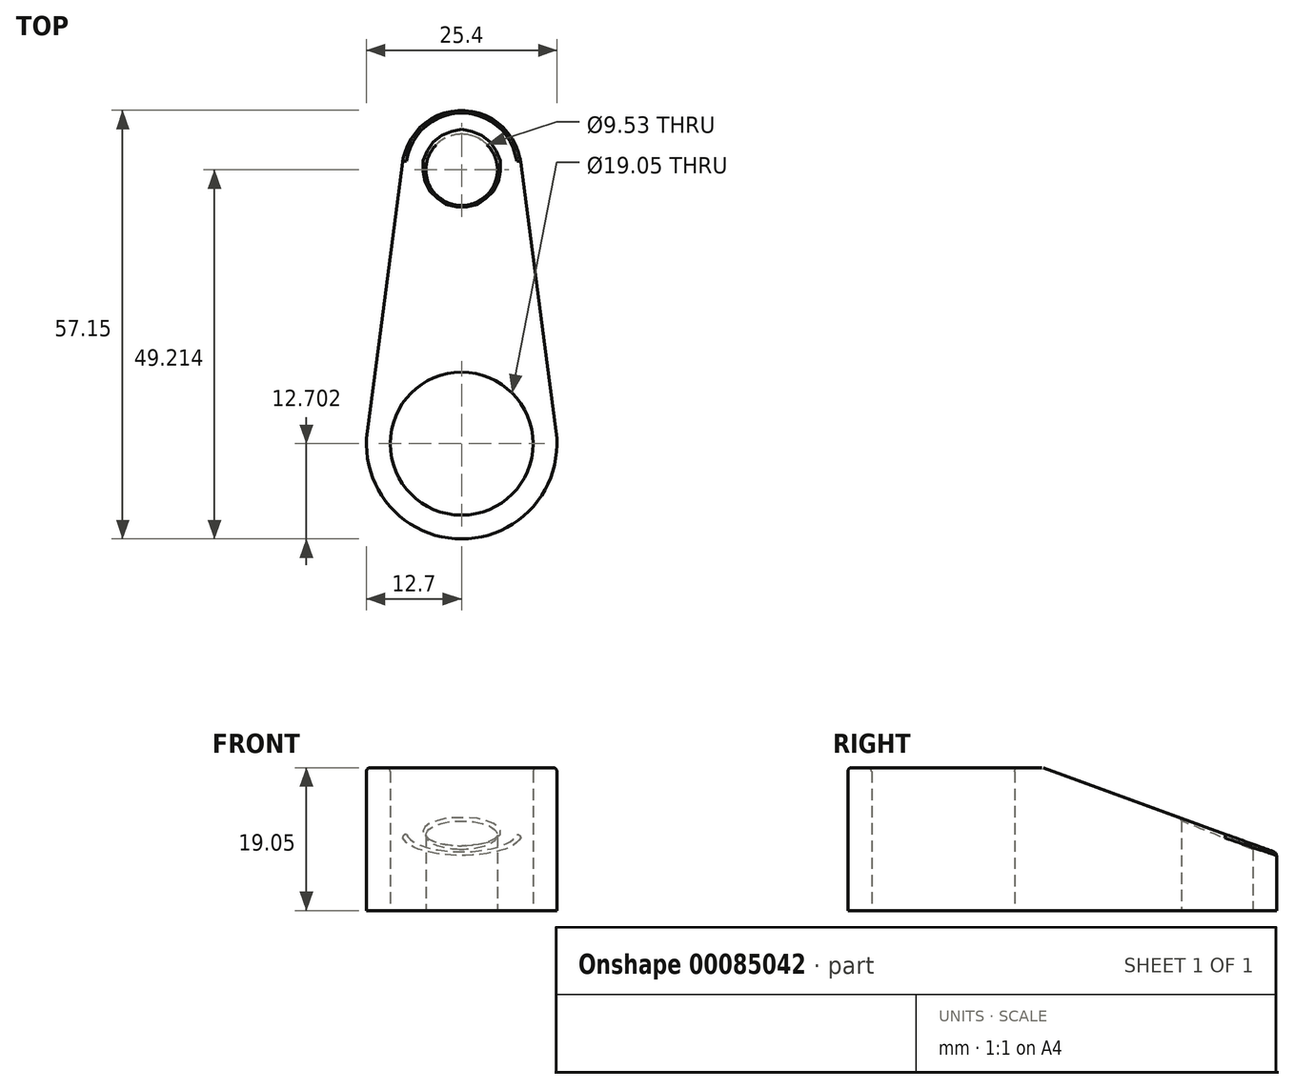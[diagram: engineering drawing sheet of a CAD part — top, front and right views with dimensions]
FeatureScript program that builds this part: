
annotation { "Feature Type Name" : "Feature", "Feature Type Description" : "" }
export const myFeature = defineFeature(function(context is Context, id is Id, definition is map)
    precondition{}
    {
        {
            var Q0;
            Q0=qCreatedBy(makeId("Top.planeOp"),FACE);
            var sketch = newSketch(context, id + "F0", { "sketchPlane" : qUnion([Q0])});
            skCircle(sketch, "E0", {"center": v(0, -23.96) * mm, "radius": 12.7 * mm});
            skCircle(sketch, "E1", {"center": v(0, 12.55) * mm, "radius": 7.94 * mm});
            skLineSegment(sketch, "E2", {"start": v(-7.87, 13.59) * mm, "end": v(-12.6, -22.3) * mm});
            skLineSegment(sketch, "E3", {"start": v(7.87, 13.59) * mm, "end": v(12.6, -22.3) * mm});
            skCircle(sketch, "E4", {"center": v(0, 12.55) * mm, "radius": 4.76 * mm});
            skCircle(sketch, "E5", {"center": v(0, -23.96) * mm, "radius": 9.53 * mm});
            skSolve(sketch);
        }
        {
            var Q0;
            {var subQ0=sQuery(id+"F0.wireOp",EDGE,"E2");Q0=makeQuery(id+"F0.imprint","IMPRINT",FACE,{"disambiguationData":[TD([[makeQuery(id+"F0.imprint","IMPRINT",EDGE,{"derivedFrom":subQ0}),1.0]])]});}
            var Q1;
            Q1=makeQuery(id+"F0.imprint","IMPRINT",FACE,{"disambiguationData":[TD([[makeQuery(id+"F0.imprint","IMPRINT",EDGE,{"derivedFrom":sQuery(id+"F0.wireOp",EDGE,"E4")}),-1.0]])]});
            var Q2;
            Q2=makeQuery(id+"F0.imprint","IMPRINT",FACE,{"disambiguationData":[TD([[makeQuery(id+"F0.imprint","IMPRINT",EDGE,{"derivedFrom":sQuery(id+"F0.wireOp",EDGE,"E5")}),-1.0]])]});
            extrude(context, id + "F1", {"entities" : qUnion([Q0, Q1, Q2]), "depth" : 19.05 * mm});
        }
        {
            var Q0;
            Q0=qCreatedBy(makeId("Right.planeOp"),FACE);
            var sketch = newSketch(context, id + "F2", { "sketchPlane" : qUnion([Q0])});
            skLineSegment(sketch, "E6", {"start": v(-25.15, 0) * mm, "end": v(-25.15, 19.55) * mm, "construction": true});
            skLineSegment(sketch, "E7", {"start": v(-12.45, 19.69) * mm, "end": v(27.54, 19.69) * mm});
            skLineSegment(sketch, "E8", {"start": v(27.54, 19.69) * mm, "end": v(27.54, 5.13) * mm});
            skLineSegment(sketch, "E9", {"start": v(27.54, 5.13) * mm, "end": v(-12.45, 19.69) * mm});
            skSolve(sketch);
        }
        {
            var Q0;
            Q0=makeQuery(id+"F2.imprint","IMPRINT",FACE,{"disambiguationData":[TD([[makeQuery(id+"F2.imprint","IMPRINT",EDGE,{"derivedFrom":sQuery(id+"F2.wireOp",EDGE,"E7")}),-1.0]])]});
            extrude(context, id + "F3", {"entities" : qUnion([Q0]), "operationType" : NewBodyOperationType.REMOVE, "endBound" : BoundingType.SYMMETRIC, "depth" : 25.4 * mm});
        }
        {
            var Q0;
            Q0=makeQuery(id+"F3.boolean.opBoolean","INTERSECT",EDGE,{"derivedFrom":[makeQuery(id+"F1.opExtrude","CAP_FACE",FACE,{"disambiguationData":[OSD([sQuery(id+"F0.wireOp",EDGE,"E0"),sQuery(id+"F0.wireOp",EDGE,"E1"),sQuery(id+"F0.wireOp",EDGE,"E2"),sQuery(id+"F0.wireOp",EDGE,"E3"),sQuery(id+"F0.wireOp",EDGE,"E4"),sQuery(id+"F0.wireOp",EDGE,"E5")])],"isStart":false}),makeQuery(id+"F3.opExtrude","SWEPT_FACE",FACE,{"disambiguationData":[OSD([sQuery(id+"F2.wireOp",EDGE,"E9")])]})]});
            var Q1;
            Q1=makeQuery(id+"F1.opExtrude","CAP_EDGE",EDGE,{"disambiguationData":[OSD([sQuery(id+"F0.wireOp",EDGE,"E0")])],"isStart":false});
            var Q2;
            Q2=makeQuery(id+"F3.boolean.opBoolean","INTERSECT",EDGE,{"derivedFrom":[makeQuery(id+"F1.opExtrude","SWEPT_FACE",FACE,{"disambiguationData":[OSD([sQuery(id+"F0.wireOp",EDGE,"E3")])]}),makeQuery(id+"F3.opExtrude","SWEPT_FACE",FACE,{"disambiguationData":[OSD([sQuery(id+"F2.wireOp",EDGE,"E9")])]})]});
            var Q3;
            Q3=makeQuery(id+"F1.opExtrude","CAP_EDGE",EDGE,{"disambiguationData":[OSD([sQuery(id+"F0.wireOp",EDGE,"E5")])],"isStart":false});
            var Q4;
            Q4=makeQuery(id+"F3.boolean.opBoolean","INTERSECT",EDGE,{"derivedFrom":[makeQuery(id+"F1.opExtrude","SWEPT_FACE",FACE,{"disambiguationData":[OSD([sQuery(id+"F0.wireOp",EDGE,"E4")])]}),makeQuery(id+"F3.opExtrude","SWEPT_FACE",FACE,{"disambiguationData":[OSD([sQuery(id+"F2.wireOp",EDGE,"E9")])]})]});
            fillet(context, id + "F4", {"entities" : qUnion([Q0, Q1, Q2, Q3, Q4]), "radius" : 0.5 * mm, "tangentPropagation" : true, "allowEdgeOverflow" : false});
        }
    });
